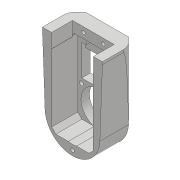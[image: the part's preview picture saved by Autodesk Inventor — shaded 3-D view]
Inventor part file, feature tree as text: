
AUTODESK INVENTOR PART (.ipt)
format: ipt  version: 2018 (Build 220112000, 112)  size: 742,912 bytes
history: native  units: mm
features: sketch x34, projected_geometry x31, extrude x27, hole x9, fillet x7, chamfer x3, mirror x1
ambient origin geometry x8: Origin, YZ Plane, XZ Plane, XY Plane, X Axis, Y Axis, Z Axis, Center Point
bodies: Solid1 (feature_tree)
feature tree (112):
  extrude  "Extrusion1"  Depth=45.0mm
  extrude  "Extrusion2"  Depth=2.25mm
  hole  "Hole1"  [1 undecoded]
  hole  "Hole2"  [1 undecoded]
  fillet  "Fillet1"  Radius=14.0mm
  extrude  "Extrusion3"  Depth=18.5mm
  extrude  "Extrusion4"  Depth=10.0mm
  extrude  "Extrusion5"  Depth=2.195mm
  extrude  "Extrusion6"  Depth=20.5mm
  hole  "Hole3"  [1 undecoded]
  extrude  "Extrusion7"  Depth=0.5mm
  extrude  "Extrusion8"  Depth=5.0mm TaperAngle=0.0deg
  extrude  "Extrusion9"  Depth=10.0mm
  extrude  "Extrusion10"  Depth=10.0mm
  extrude  "Extrusion11"  Depth=14.5mm
  extrude  "Extrusion12"  Depth=14.5mm
  extrude  "Extrusion13"  Depth=5.0mm
  extrude  "Extrusion14"  Depth=2.25mm
  extrude  "Extrusion15"  Depth=5.0mm
  extrude  "Extrusion16"  Depth=9.0mm
  extrude  "Extrusion17"  Depth=4.0mm
  chamfer  "Chamfer1"  Distance=1.0mm
  fillet  "Fillet7"  Radius=20.7mm
  fillet  "Fillet8"  Radius=32.0mm
  mirror  "Mirror1"
  extrude  "Extrusion19"  Depth=1.0mm TaperAngle=0.0deg
  extrude  "Extrusion20"  Depth=8.0mm
  extrude  "Extrusion21"  Depth=0.2mm TaperAngle=0.0deg
  extrude  "Extrusion22"  Depth=0.5mm TaperAngle=0.0deg
  extrude  "Extrusion23"  Depth=5.0mm TaperAngle=0.0deg
  chamfer  "Chamfer2"  Distance=5.0mm
  fillet  "Fillet9"  Radius=0.2mm
  extrude  "Extrusion24"  Depth=2.5mm TaperAngle=45.0deg
  extrude  "Extrusion27"  Depth=0.5mm
  extrude  "Extrusion28"  Depth=1.8mm TaperAngle=0.0deg
  hole  "Hole6"  [1 undecoded]
  sketch  "Sketch39"  dims[d105=1.5mm d114=0.5mm]
  hole  "Hole7"  [1 undecoded]
  hole  "Hole8"  [1 undecoded]
  fillet  "Fillet10"  Radius=5.0mm
  hole  "Hole9"  [1 undecoded]
  extrude  "Extrusion29"  Depth=10.0mm
  chamfer  "Chamfer4"  Distance=10.0mm
  hole  "Hole10"  [1 undecoded]
  fillet  "Fillet11"  Radius=18.0mm
  hole  "Hole11"  [1 undecoded]
  fillet  "Fillet12"  Radius=0.05mm
  extrude  "Extrusion30"  Depth=10.0mm TaperAngle=0.0deg
  sketch  "Sketch1"  dims[d0=24.5mm d1=45.0mm]
  sketch  "Sketch2"  dims[d2=1.95mm d3=0.0mm d4=2.25mm]
  projected_geometry  "Projected Loop1"
  sketch  "Sketch3"  dims[d5=20.0mm d6=2.25mm]
  projected_geometry  "Projected Loop2"
  sketch  "Sketch4"  dims[d7=5.25mm d8=5.25mm d9=14.0mm]
  projected_geometry  "Projected Loop3"
  sketch  "Sketch5"  dims[d10=5.25mm d11=18.5mm]
  projected_geometry  "Projected Loop4"
  sketch  "Sketch6"  dims[d12=10.0mm d13=0.0mm d14=20.5mm]
  projected_geometry  "Projected Loop5"
  sketch  "Sketch7"  dims[d15=2.0mm d16=2.195mm]
  projected_geometry  "Projected Loop6"
  sketch  "Sketch8"  dims[d17=2.0mm]
  projected_geometry  "Projected Loop7"
  sketch  "Sketch9"  dims[d18=2.4mm d19=6.0mm d20=4.4mm d21=2.0mm d22=90.0deg d23=8.0mm d24=20.594885mm d25=20.5mm]
  projected_geometry  "Projected Loop8"
  projected_geometry  "Projected Loop9"
  sketch  "Sketch10"  dims[d26=26.65mm d27=2.0mm]
  projected_geometry  "Projected Loop10"
  projected_geometry  "Projected Loop11"
  sketch  "Sketch11"  dims[d28=2.0mm]
  projected_geometry  "Projected Loop12"
  sketch  "Sketch12"  dims[d29=2.4mm d30=6.0mm d31=4.4mm d32=2.0mm d33=90.0deg d34=8.0mm d35=20.594885mm d36=0.5mm]
  sketch  "Sketch13"  dims[d37=18.0mm d38=5.0mm d39=0.0mm]
  sketch  "Sketch14"  dims[d41=10.0mm d42=0.0mm d43=24.5mm]
  projected_geometry  "Projected Loop13"
  sketch  "Sketch15"  dims[d44=1.15mm d45=0.0mm d46=10.0mm]
  sketch  "Sketch16"  dims[d47=21.0mm d48=14.5mm]
  projected_geometry  "Projected Loop14"
  sketch  "Sketch17"  dims[d49=20.0mm d50=14.5mm]
  projected_geometry  "Projected Loop15"
  sketch  "Sketch18"  dims[d51=24.5mm d52=5.0mm]
  projected_geometry  "Projected Loop16"
  sketch  "Sketch19"  dims[d53=5.0mm d54=2.25mm]
  projected_geometry  "Projected Loop17"
  sketch  "Sketch20"  dims[d55=2.25mm d56=5.0mm]
  projected_geometry  "Projected Loop18"
  sketch  "Sketch25"  dims[d57=5.0mm d58=9.0mm]
  projected_geometry  "Projected Loop22"
  sketch  "Sketch26"  dims[d59=14.75mm d60=4.0mm d61=1.0mm d62=0.0mm d63=20.7mm]
  projected_geometry  "Projected Loop23"
  sketch  "Sketch27"  dims[d64=2.4mm d65=6.0mm d66=4.4mm d67=2.0mm d68=90.0deg d69=8.0mm d70=20.594885mm d72=32.0mm]
  projected_geometry  "Projected Loop25"
  sketch  "Sketch29"  dims[d73=5.0mm d74=0.0mm d75=1.0mm d76=0.0mm]
  projected_geometry  "Projected Loop26"
  sketch  "Sketch30"  dims[d77=12.25mm d78=0.0mm d80=8.0mm]
  projected_geometry  "Projected Loop27"
  sketch  "Sketch32"  dims[d81=4.5mm d82=0.0mm d84=0.2mm d85=0.0mm]
  projected_geometry  "Projected Loop28"
  projected_geometry  "Projected Loop29"
  sketch  "Sketch36"  dims[d86=21.0mm d87=0.5mm d88=0.0mm]
  projected_geometry  "Projected Loop33"
  sketch  "Sketch37"  dims[d91=8.0mm d92=0.0mm d93=5.0mm d94=0.0mm d95=5.0mm d96=0.0mm d98=0.2mm d99=0.0mm]
  projected_geometry  "Projected Loop34"
  sketch  "Sketch38"  dims[d100=0.2mm d101=0.0mm d102=2.5mm d103=2.0mm d104=45.0deg]
  projected_geometry  "Projected Loop35"
  sketch  "Sketch41"  dims[d128=1.8mm d129=0.0mm d130=1.8mm d131=0.0mm]
  projected_geometry  "Projected Loop36"
  sketch  "Sketch42"  dims[d133=36.055mm d134=4.2225mm]
  projected_geometry  "Projected Loop37"
  sketch  "Sketch43"  dims[d135=4.2225mm d136=2.0mm d137=0.0mm]
  projected_geometry  "Projected Loop38"
  sketch  "Sketch44"  dims[d138=2.0mm d139=0.0mm d140=2.0mm d141=0.0mm d142=5.0mm d143=2.0mm d144=45.0deg d145=8.0mm d147=33.0mm d148=10.0mm d149=0.0mm d161=20.75mm d162=18.0mm d163=25.0mm d164=0.05mm d165=7.0mm d166=0.0mm d167=1.5mm d168=0.0mm d169=3.0mm d170=12.0mm d171=2.1mm d172=6.0mm d173=6.3mm d174=2.0mm d175=90.0deg d176=8.0mm d177=20.594885mm d178=1.567mm d179=36.0mm d180=4.4mm d181=2.0mm d182=90.0deg d183=36.0mm d184=20.594885mm d185=4.0mm d186=5.029mm d187=4.4mm d188=2.0mm d189=90.0deg d190=15.0mm d191=0.0mm d192=0.5mm d193=2.1mm d194=5.029mm d195=4.4mm d196=2.0mm d197=90.0deg d198=20.75mm d199=0.0mm d200=15.0mm d201=1.5mm d202=0.0mm d203=1.5mm d204=2.0mm d205=45.0deg d206=4.0mm d207=5.029mm d208=4.4mm d209=2.0mm d210=90.0deg d211=2.2mm d212=0.0mm d213=0.75mm d214=4.0mm d215=5.029mm d216=4.4mm d217=2.0mm d218=90.0deg d219=2.2mm d220=0.0mm d221=0.75mm d222=20.75mm d223=0.0mm]
note: 9 required parameter values undecoded (feature->parameter linkage not recoverable at this tier; creation-order binding heuristic only, values carry confidence <= 0.55)
